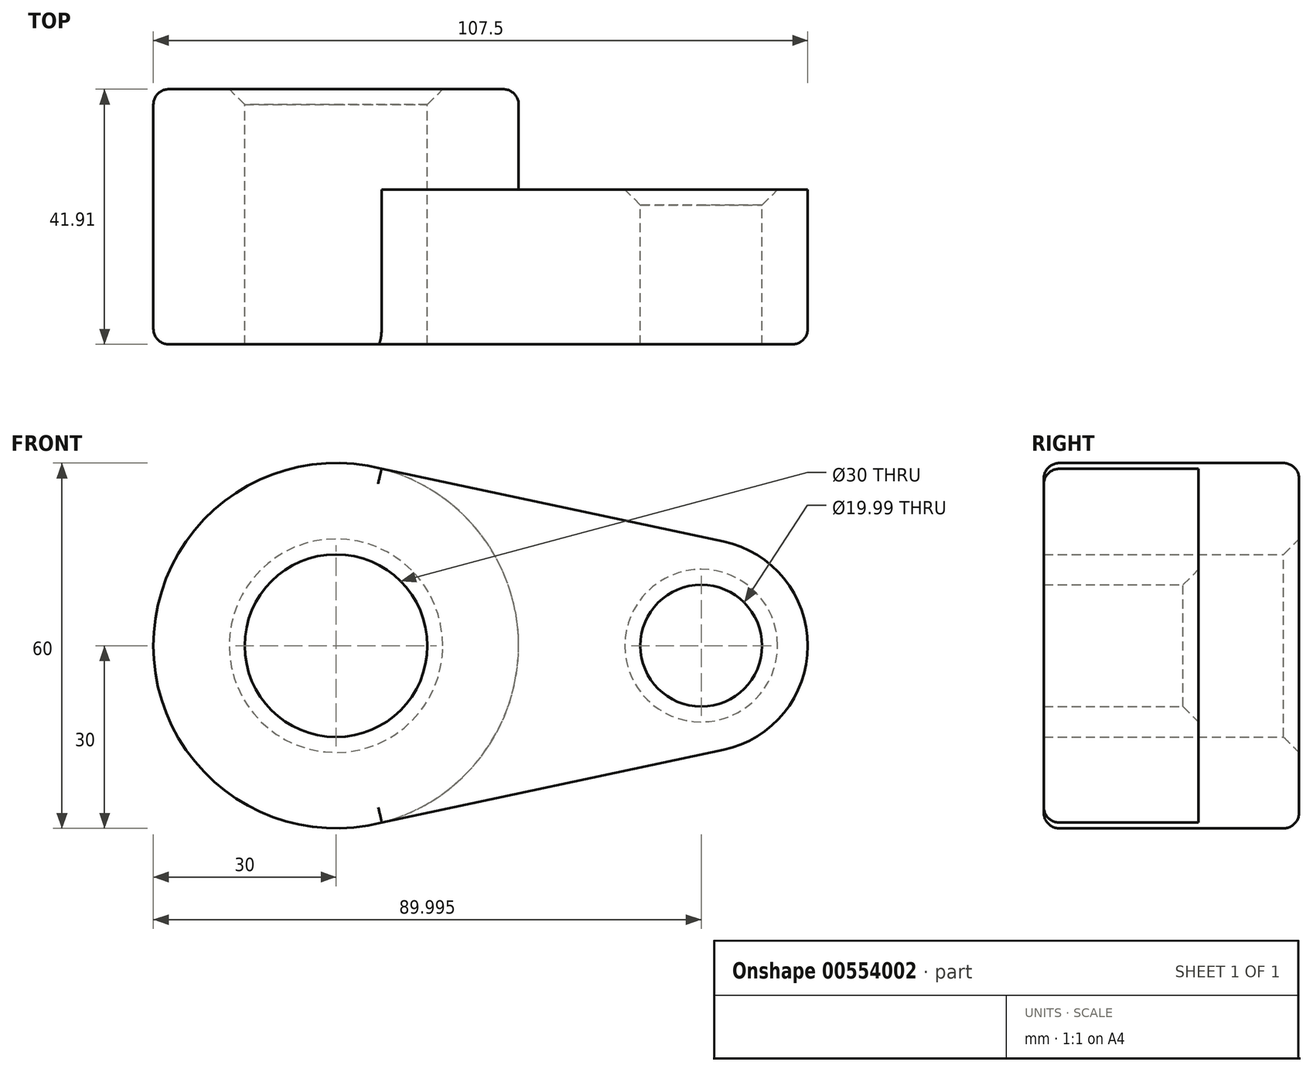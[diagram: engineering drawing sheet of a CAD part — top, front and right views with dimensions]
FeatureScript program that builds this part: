
annotation { "Feature Type Name" : "Feature", "Feature Type Description" : "" }
export const myFeature = defineFeature(function(context is Context, id is Id, definition is map)
    precondition{}
    {
        {
            var Q0;
            Q0=qCreatedBy(makeId("Front.planeOp"),FACE);
            var sketch = newSketch(context, id + "F0", { "sketchPlane" : qUnion([Q0])});
            skCircle(sketch, "E0", {"center": v(0, 0) * mm, "radius": 30 * mm});
            skCircle(sketch, "E1", {"center": v(60, 0) * mm, "radius": 17.5 * mm});
            skCircle(sketch, "E2", {"center": v(0, 0) * mm, "radius": 15 * mm});
            skCircle(sketch, "E3", {"center": v(60, 0) * mm, "radius": 10 * mm});
            skLineSegment(sketch, "E4", {"start": v(7.48, 29.05) * mm, "end": v(63.63, 17.12) * mm});
            skLineSegment(sketch, "E5", {"start": v(7.53, -29.04) * mm, "end": v(63.63, -17.12) * mm});
            skSolve(sketch);
        }
        {
            var Q0;
            Q0=makeQuery(id+"F0.imprint","IMPRINT",FACE,{"disambiguationData":[TD([[makeQuery(id+"F0.imprint","IMPRINT",EDGE,{"derivedFrom":sQuery(id+"F0.wireOp",EDGE,"E2")}),-1.0]])]});
            var Q1;
            {var subQ0=sQuery(id+"F0.wireOp",EDGE,"E4");Q1=makeQuery(id+"F0.imprint","IMPRINT",FACE,{"disambiguationData":[TD([[makeQuery(id+"F0.imprint","IMPRINT",EDGE,{"derivedFrom":subQ0}),-1.0]])]});}
            var Q2;
            Q2=makeQuery(id+"F0.imprint","IMPRINT",FACE,{"disambiguationData":[TD([[makeQuery(id+"F0.imprint","IMPRINT",EDGE,{"derivedFrom":sQuery(id+"F0.wireOp",EDGE,"E3")}),-1.0]])]});
            extrude(context, id + "F1", {"entities" : qUnion([Q0, Q1, Q2]), "depth" : 25.4 * mm, "offsetDistance" : 25.4 * mm});
        }
        {
            var Q0;
            Q0=makeQuery(id+"F0.imprint","IMPRINT",FACE,{"disambiguationData":[TD([[makeQuery(id+"F0.imprint","IMPRINT",EDGE,{"derivedFrom":sQuery(id+"F0.wireOp",EDGE,"E2")}),-1.0]])]});
            extrude(context, id + "F2", {"entities" : qUnion([Q0]), "operationType" : NewBodyOperationType.ADD, "oppositeDirection" : true, "depth" : 16.5 * mm, "offsetDistance" : 25.4 * mm});
        }
        {
            var Q0;
            Q0=makeQuery(id+"F1.opExtrude","CAP_EDGE",EDGE,{"disambiguationData":[OSD([sQuery(id+"F0.wireOp",EDGE,"E3")])],"isStart":true});
            var Q1;
            Q1=makeQuery(id+"F2.opExtrude","CAP_EDGE",EDGE,{"disambiguationData":[OSD([sQuery(id+"F0.wireOp",EDGE,"E2")])],"isStart":false});
            chamfer(context, id + "F3", {"entities" : qUnion([Q0, Q1]), "width" : 2.54 * mm, "tangentPropagation" : true});
        }
        {
            var Q0;
            Q0=makeQuery(id+"F2.opExtrude","CAP_EDGE",EDGE,{"disambiguationData":[OSD([sQuery(id+"F0.wireOp",EDGE,"E0")])],"isStart":false});
            var Q1;
            Q1=makeQuery(id+"F1.opExtrude","CAP_EDGE",EDGE,{"disambiguationData":[OSD([sQuery(id+"F0.wireOp",EDGE,"E4")])],"isStart":false});
            var Q2;
            Q2=makeQuery(id+"F1.opExtrude","CAP_EDGE",EDGE,{"disambiguationData":[OSD([sQuery(id+"F0.wireOp",EDGE,"E1")])],"isStart":false});
            var Q3;
            Q3=makeQuery(id+"F1.opExtrude","CAP_EDGE",EDGE,{"disambiguationData":[OSD([sQuery(id+"F0.wireOp",EDGE,"E0")])],"isStart":false});
            var Q4;
            Q4=makeQuery(id+"F1.opExtrude","CAP_EDGE",EDGE,{"disambiguationData":[OSD([sQuery(id+"F0.wireOp",EDGE,"E5")])],"isStart":false});
            fillet(context, id + "F4", {"entities" : qUnion([Q0, Q1, Q2, Q3, Q4]), "radius" : 2.54 * mm, "tangentPropagation" : true, "allowEdgeOverflow" : false});
        }
    });
